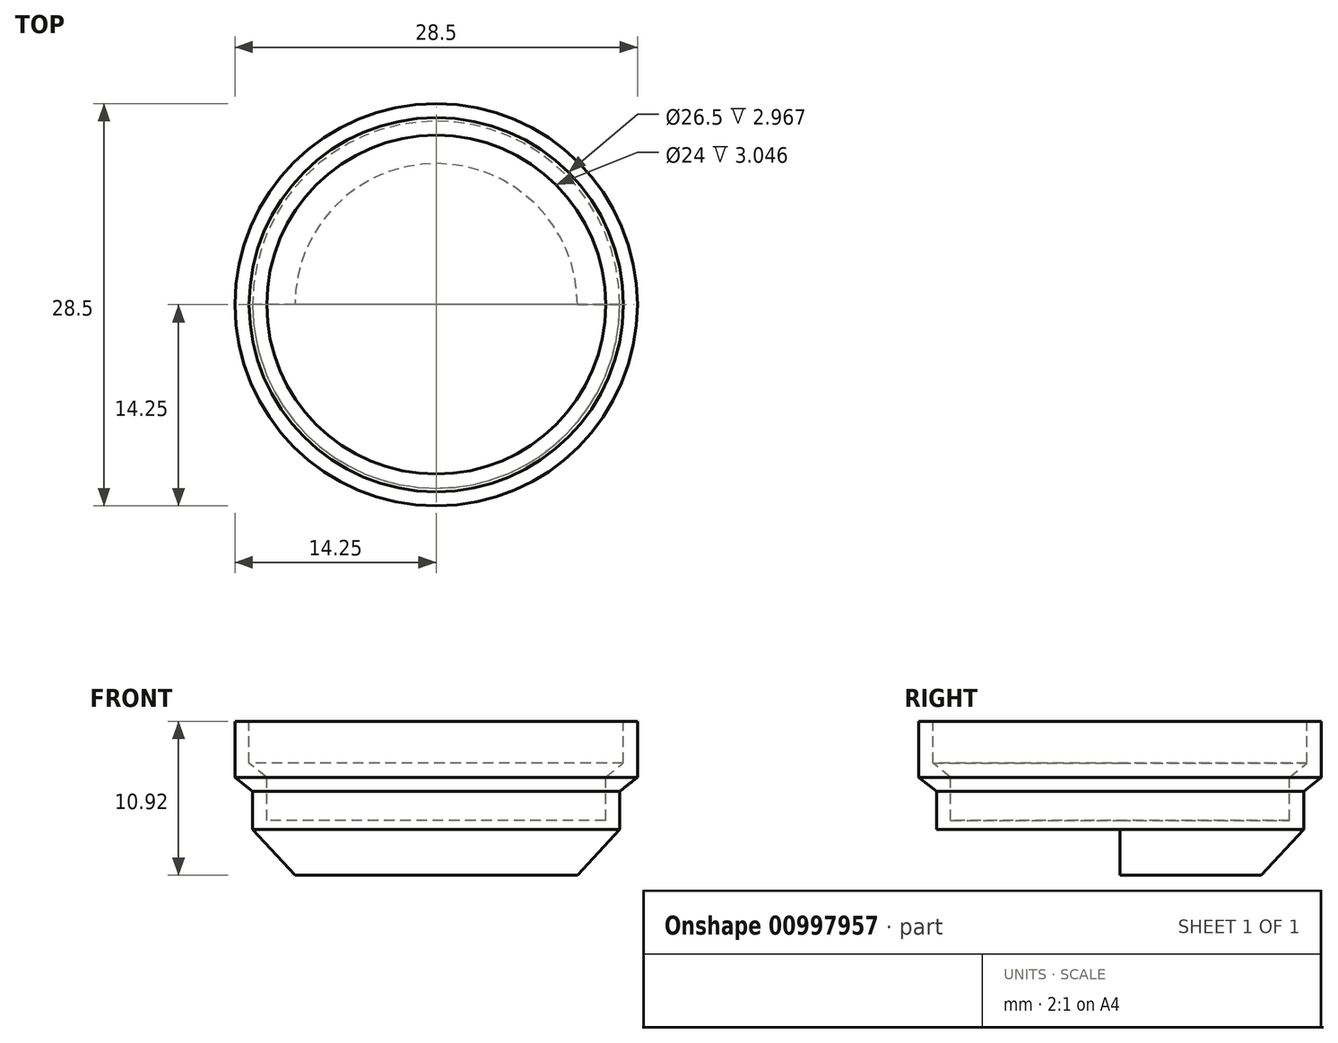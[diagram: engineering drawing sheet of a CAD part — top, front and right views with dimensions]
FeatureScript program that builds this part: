
annotation { "Feature Type Name" : "Feature", "Feature Type Description" : "" }
export const myFeature = defineFeature(function(context is Context, id is Id, definition is map)
    precondition{}
    {
        {
            var Q0;
            Q0=qCreatedBy(makeId("Front.planeOp"),FACE);
            var sketch = newSketch(context, id + "F0", { "sketchPlane" : qUnion([Q0])});
            skLineSegment(sketch, "E0", {"start": v(0, 0) * mm, "end": v(0, 6.56) * mm, "construction": true});
            skLineSegment(sketch, "E1", {"start": v(13.25, 3.97) * mm, "end": v(14.25, 3.97) * mm});
            skLineSegment(sketch, "E2", {"start": v(14.25, 3.97) * mm, "end": v(14.25, 0) * mm});
            skLineSegment(sketch, "E3", {"start": v(12, 0) * mm, "end": v(13.25, 1) * mm});
            skLineSegment(sketch, "E4", {"start": v(14.25, 0) * mm, "end": v(13, -1) * mm});
            skLineSegment(sketch, "E5", {"start": v(13.25, 3.97) * mm, "end": v(13.25, 1) * mm});
            skLineSegment(sketch, "E6", {"start": v(13, -1) * mm, "end": v(13, -3.7) * mm});
            skLineSegment(sketch, "E7", {"start": v(12, -3.7) * mm, "end": v(0, -3.7) * mm});
            skLineSegment(sketch, "E8", {"start": v(0, -3.7) * mm, "end": v(0, -6.95) * mm});
            skLineSegment(sketch, "E9", {"start": v(0, -6.95) * mm, "end": v(10, -6.95) * mm});
            skLineSegment(sketch, "E10", {"start": v(10, -6.95) * mm, "end": v(13, -3.7) * mm});
            skLineSegment(sketch, "E11", {"start": v(12, -3.7) * mm, "end": v(13, -3.7) * mm});
            skLineSegment(sketch, "E12", {"start": v(12, -3.05) * mm, "end": v(0, -3.05) * mm});
            skLineSegment(sketch, "E13", {"start": v(0, -3.05) * mm, "end": v(0, -3.7) * mm});
            skLineSegment(sketch, "E14", {"start": v(12, 0) * mm, "end": v(12, -3.05) * mm});
            skSolve(sketch);
        }
        {
            var Q0;
            Q0=makeQuery(id+"F0.imprint","IMPRINT",FACE,{"disambiguationData":[TD([[makeQuery(id+"F0.imprint","IMPRINT",EDGE,{"derivedFrom":sQuery(id+"F0.wireOp",EDGE,"E1")}),-1.0]])]});
            var Q1;
            Q1=makeQuery(id+"F0.imprint","IMPRINT",FACE,{"disambiguationData":[TD([[makeQuery(id+"F0.imprint","IMPRINT",EDGE,{"derivedFrom":sQuery(id+"F0.wireOp",EDGE,"E1")}),-1.0]])]});
            var Q2;
            Q2=makeQuery(id+"F0.imprint","IMPRINT",FACE,{"disambiguationData":[TD([[makeQuery(id+"F0.imprint","IMPRINT",EDGE,{"derivedFrom":sQuery(id+"F0.wireOp",EDGE,"E1")}),-1.0]])]});
            var Q3;
            Q3=sQuery(id+"F0.wireOp",EDGE,"E13");
            revolve(context, id + "F1", {"surfaceOperationType" : NewSurfaceOperationType.NEW, "entities" : qUnion([Q0, Q1, Q2]), "axis" : qUnion([Q3]), "revolveType" : RevolveType.FULL});
        }
        {
            var Q0;
            Q0=makeQuery(id+"F0.imprint","IMPRINT",FACE,{"disambiguationData":[TD([[makeQuery(id+"F0.imprint","IMPRINT",EDGE,{"derivedFrom":sQuery(id+"F0.wireOp",EDGE,"E7")}),1.0]])]});
            var Q1;
            Q1=sQuery(id+"F0.wireOp",EDGE,"E0");
            revolve(context, id + "F2", {"operationType" : NewBodyOperationType.ADD, "surfaceOperationType" : NewSurfaceOperationType.NEW, "entities" : qUnion([Q0]), "axis" : qUnion([Q1]), "revolveType" : RevolveType.ONE_DIRECTION, "angle" : 180 * degree});
        }
    });
